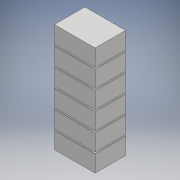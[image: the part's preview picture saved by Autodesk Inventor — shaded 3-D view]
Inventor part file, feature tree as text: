
AUTODESK INVENTOR PART (.ipt)
format: ipt  version: 2018 (Build 220112000, 112)  size: 112,640 bytes
history: native  units: mm
features: extrude x1, pattern_linear x1, sketch x1
ambient origin geometry x8: Origin, YZ Plane, XZ Plane, XY Plane, X Axis, Y Axis, Z Axis, Center Point
bodies: Solid1 (feature_tree)
feature tree (3):
  extrude  "Extrusion1"  Depth=45.0mm
  pattern_linear  "Rectangular Pattern1"  Spacing1=25.0mm  [1 undecoded]
  sketch  "Sketch1"  dims[d0=60.0mm d1=45.0mm d2=25.0mm d3=0.0mm d4=60.0mm d6=135.0mm]
note: 1 required parameter value undecoded (feature->parameter linkage not recoverable at this tier; creation-order binding heuristic only, values carry confidence <= 0.55)
